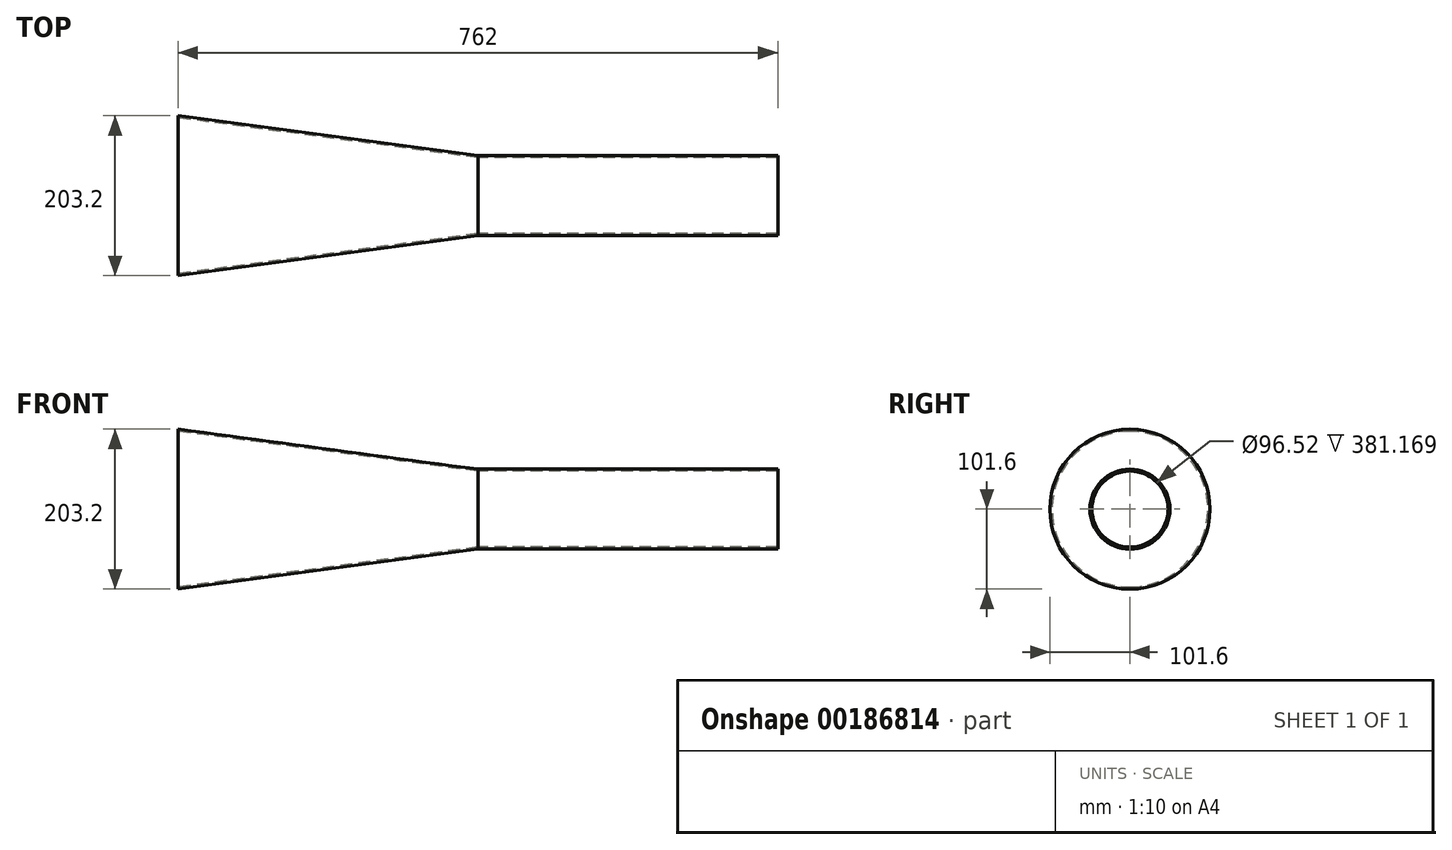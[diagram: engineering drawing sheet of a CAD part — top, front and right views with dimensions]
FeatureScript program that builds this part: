
annotation { "Feature Type Name" : "Feature", "Feature Type Description" : "" }
export const myFeature = defineFeature(function(context is Context, id is Id, definition is map)
    precondition{}
    {
        {
            var Q0;
            Q0=qCreatedBy(makeId("Front.planeOp"),FACE);
            var sketch = newSketch(context, id + "F0", { "sketchPlane" : qUnion([Q0])});
            skLineSegment(sketch, "E0", {"start": v(-381, 0) * mm, "end": v(381, 0) * mm});
            skLineSegment(sketch, "E1", {"start": v(381, 0) * mm, "end": v(381, 50.8) * mm});
            skLineSegment(sketch, "E2", {"start": v(381, 50.8) * mm, "end": v(0, 50.8) * mm});
            skLineSegment(sketch, "E3", {"start": v(0, 50.8) * mm, "end": v(-381, 101.6) * mm});
            skLineSegment(sketch, "E4", {"start": v(-381, 101.6) * mm, "end": v(-381, 0) * mm});
            skSolve(sketch);
        }
        {
            var Q0;
            Q0=makeQuery(id+"F0.imprint","IMPRINT",FACE,{"disambiguationData":[TD([[makeQuery(id+"F0.imprint","IMPRINT",EDGE,{"derivedFrom":sQuery(id+"F0.wireOp",EDGE,"E0")}),1.0]])]});
            var Q1;
            Q1=sQuery(id+"F0.wireOp",EDGE,"E0");
            revolve(context, id + "F1", {"entities" : qUnion([Q0]), "axis" : qUnion([Q1]), "revolveType" : RevolveType.FULL});
        }
        {
            var Q0;
            Q0=makeQuery(id+"F1.opRevolve","SWEPT_FACE",FACE,{"disambiguationData":[OSD([sQuery(id+"F0.wireOp",EDGE,"E4")])]});
            var Q1;
            Q1=makeQuery(id+"F1.opRevolve","SWEPT_FACE",FACE,{"disambiguationData":[OSD([sQuery(id+"F0.wireOp",EDGE,"E1")])]});
            shell(context, id + "F2", {"entities" : qUnion([Q0, Q1]), "thickness" : 2.54 * mm});
        }
    });
